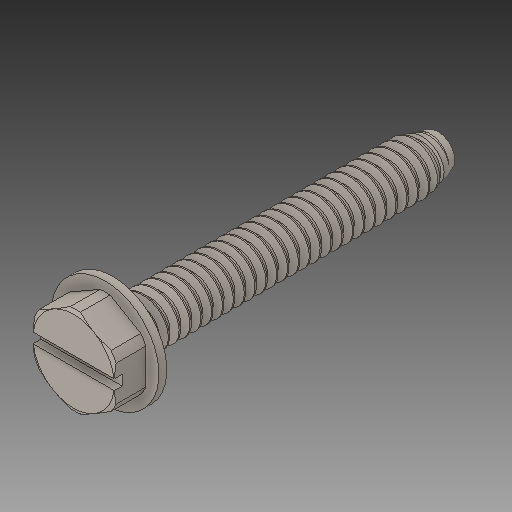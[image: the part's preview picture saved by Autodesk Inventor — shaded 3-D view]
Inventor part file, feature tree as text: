
AUTODESK INVENTOR PART (.ipt)
format: ipt  version: 2018.2 (Build 222227000, 227)  size: 798,208 bytes
history: native  units: in
note: dims shown in document units (in); Inventor stores cm internally (conversion verified against a paired STEP export)
features: extrude x1
ambient origin geometry x8: Origin, YZ Plane, XZ Plane, XY Plane, X Axis, Y Axis, Z Axis, Center Point
bodies: Solid1 (feature_tree)
feature tree (1):
  extrude  "Extrude4"  [1 undecoded]
note: 1 required parameter value undecoded (feature->parameter linkage not recoverable at this tier; creation-order binding heuristic only, values carry confidence <= 0.55)
